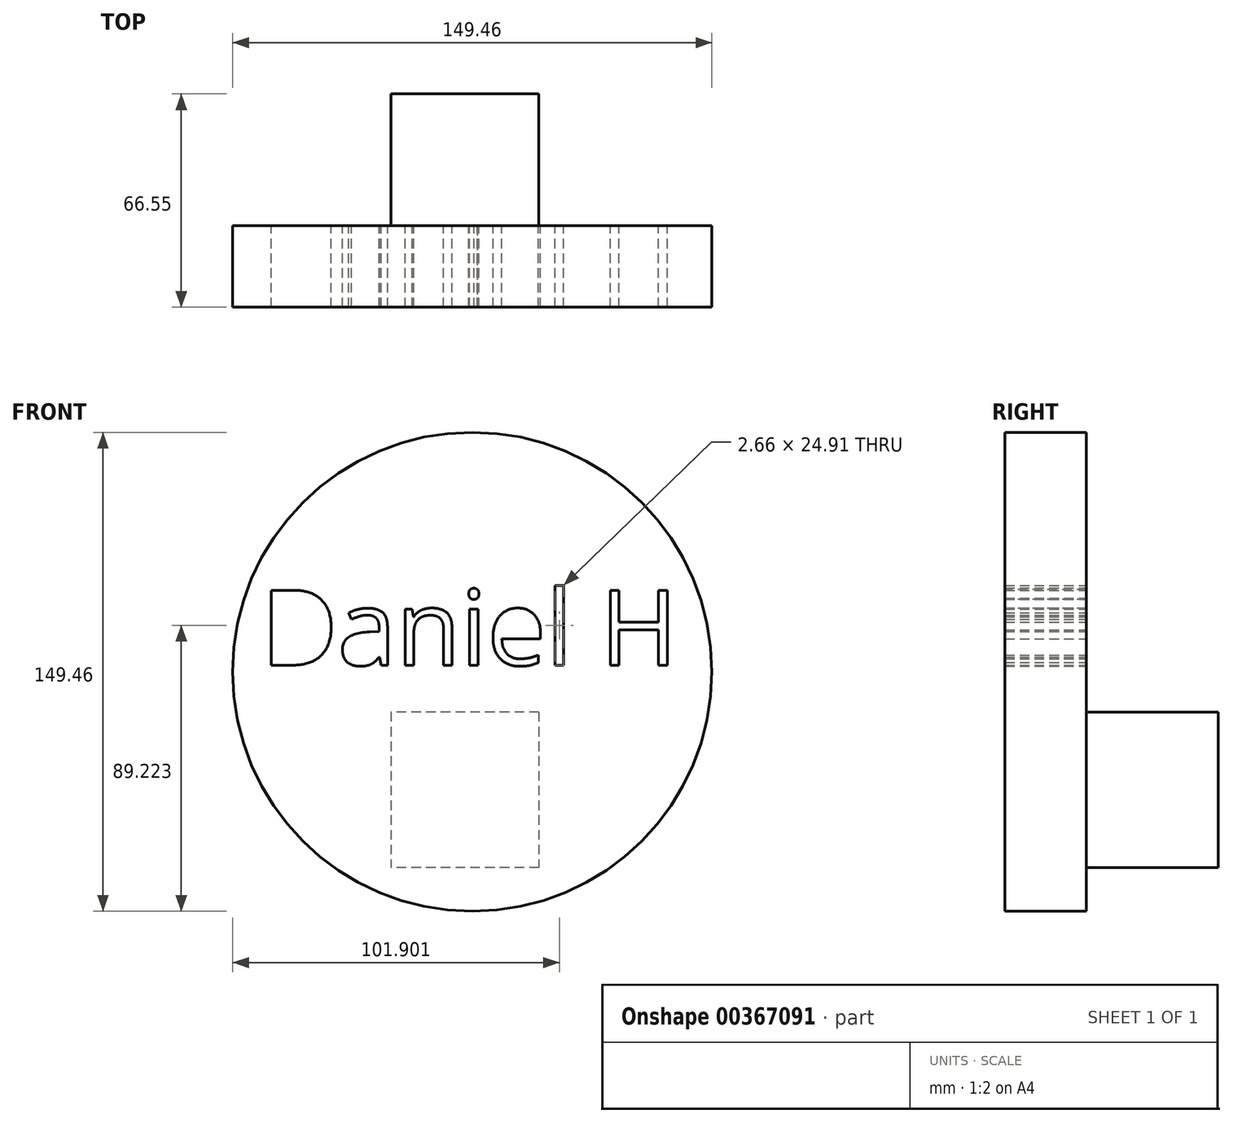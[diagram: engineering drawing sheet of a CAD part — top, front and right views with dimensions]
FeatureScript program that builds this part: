
annotation { "Feature Type Name" : "Feature", "Feature Type Description" : "" }
export const myFeature = defineFeature(function(context is Context, id is Id, definition is map)
    precondition{}
    {
        {
            var Q0;
            Q0=qCreatedBy(makeId("Front.planeOp"),FACE);
            var sketch = newSketch(context, id + "F0", { "sketchPlane" : qUnion([Q0])});
            skCircle(sketch, "E0", {"center": v(0, 0) * mm, "radius": 74.73 * mm});
            skText(sketch, "E1", { "text": "Daniel H", "fontName": "OpenSans-Regular.ttf"});
            const initialGuessF0  = {"E1": [-0.0659, 0.00204, 1, 0, 0.0236]};
            skSetInitialGuess(sketch, initialGuessF0);
            skSolve(sketch);
        }
        {
            var Q0;
            Q0=makeQuery(id+"F0.imprint","IMPRINT",FACE,{"disambiguationData":[TD([[makeQuery(id+"F0.imprint","IMPRINT",EDGE,{"derivedFrom":sQuery(id+"F0.wireOp",EDGE,"E0")}),1.0]])]});
            var sketch = newSketch(context, id + "F1", { "sketchPlane" : qUnion([Q0])});
            skLineSegment(sketch, "E2.bottom", {"start": v(20.8, -12.54) * mm, "end": v(-25.35, -12.54) * mm});
            skLineSegment(sketch, "E2.top", {"start": v(20.8, -61.05) * mm, "end": v(-25.35, -61.05) * mm});
            skLineSegment(sketch, "E2.left", {"start": v(20.8, -12.54) * mm, "end": v(20.8, -61.05) * mm});
            skLineSegment(sketch, "E2.right", {"start": v(-25.35, -12.54) * mm, "end": v(-25.35, -61.05) * mm});
            skSolve(sketch);
        }
        {
            var Q0;
            Q0=qSketchRegion(id+"F0",true);
            extrude(context, id + "F2", {"entities" : qUnion([Q0]), "depth" : 25.4 * mm});
        }
        {
            var Q0;
            Q0=makeQuery(id+"F1.imprint","IMPRINT",FACE,{"disambiguationData":[TD([[makeQuery(id+"F1.imprint","IMPRINT",EDGE,{"derivedFrom":sQuery(id+"F1.wireOp",EDGE,"E2.bottom")}),1.0]])]});
            extrude(context, id + "F3", {"entities" : qUnion([Q0]), "operationType" : NewBodyOperationType.ADD, "oppositeDirection" : true, "depth" : 41.15 * mm});
        }
    });
